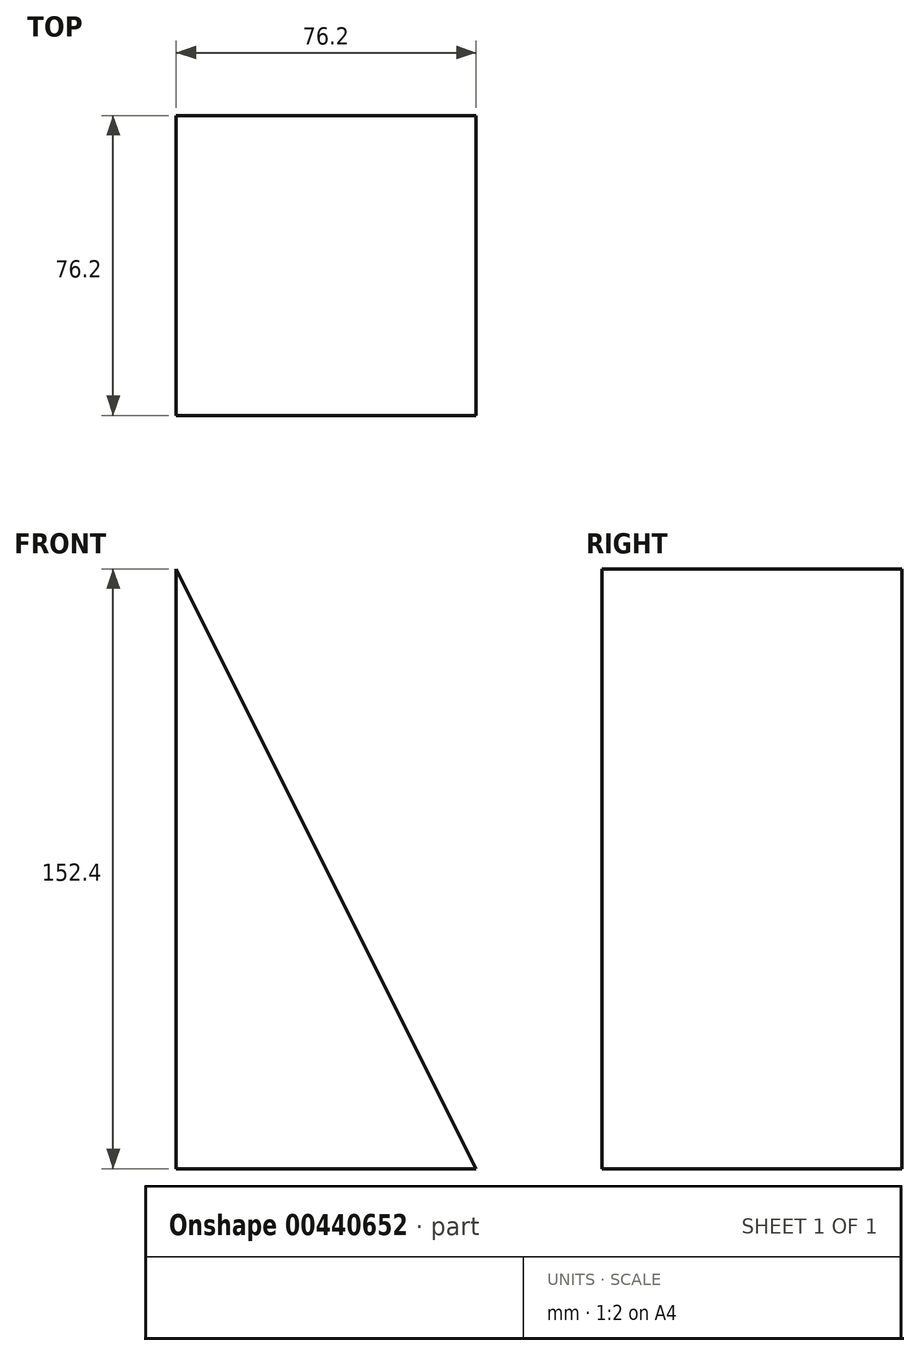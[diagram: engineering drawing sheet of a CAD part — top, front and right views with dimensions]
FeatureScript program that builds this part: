
annotation { "Feature Type Name" : "Feature", "Feature Type Description" : "" }
export const myFeature = defineFeature(function(context is Context, id is Id, definition is map)
    precondition{}
    {
        {
            var Q0;
            Q0=qCreatedBy(makeId("Front.planeOp"),FACE);
            var sketch = newSketch(context, id + "F0", { "sketchPlane" : qUnion([Q0])});
            skLineSegment(sketch, "E0", {"start": v(0, 0) * mm, "end": v(0, 152.4) * mm});
            skLineSegment(sketch, "E1", {"start": v(0, 152.4) * mm, "end": v(76.2, 0) * mm});
            skLineSegment(sketch, "E2", {"start": v(76.2, 0) * mm, "end": v(0, 0) * mm});
            skSolve(sketch);
        }
        {
            var Q0;
            Q0=makeQuery(id+"F0.imprint","IMPRINT",FACE,{"disambiguationData":[TD([[makeQuery(id+"F0.imprint","IMPRINT",EDGE,{"derivedFrom":sQuery(id+"F0.wireOp",EDGE,"E0")}),-1.0]])]});
            extrude(context, id + "F1", {"entities" : qUnion([Q0]), "depth" : 76.2 * mm});
        }
    });
